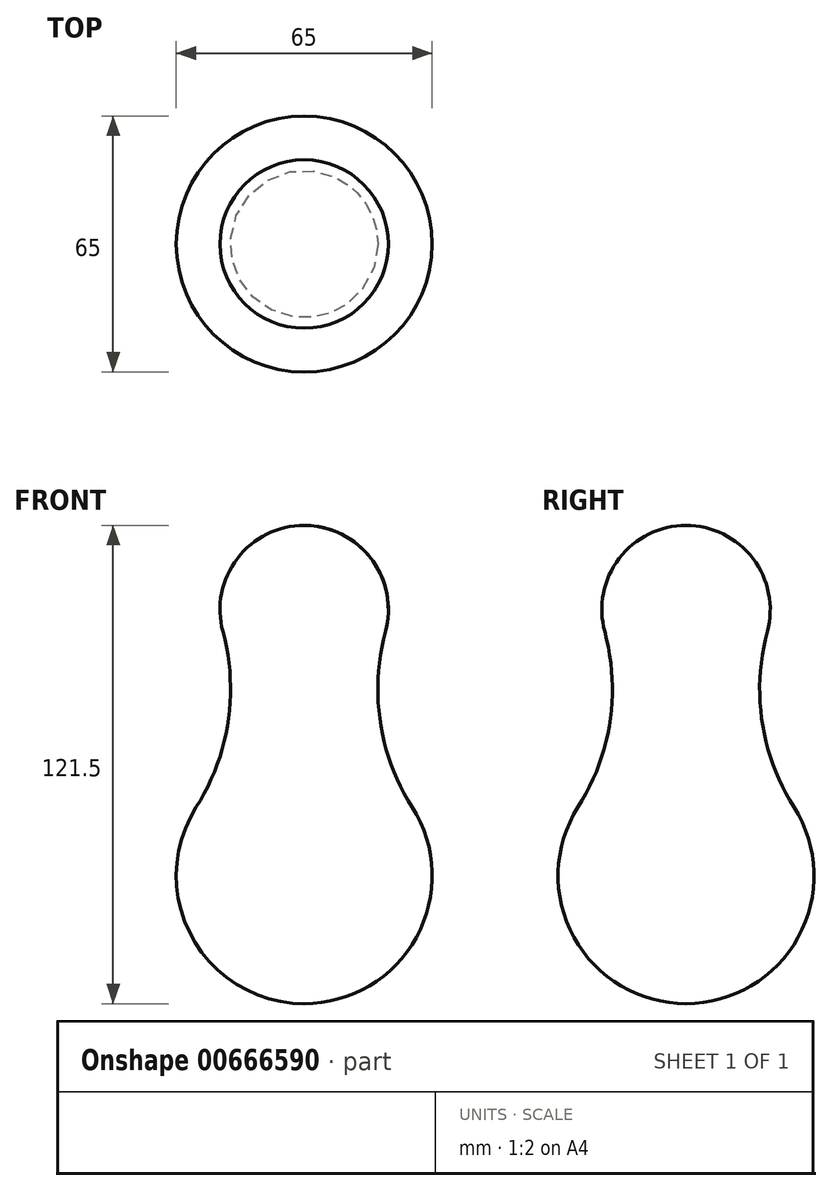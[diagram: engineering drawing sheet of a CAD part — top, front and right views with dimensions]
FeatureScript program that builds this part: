
annotation { "Feature Type Name" : "Feature", "Feature Type Description" : "" }
export const myFeature = defineFeature(function(context is Context, id is Id, definition is map)
    precondition{}
    {
        {
            var Q0;
            Q0=qCreatedBy(makeId("Front.planeOp"),FACE);
            var sketch = newSketch(context, id + "F0", { "sketchPlane" : qUnion([Q0])});
            skArc(sketch, "E0", {"start": v(0, 54.91) * mm, "mid": v(-16.99, 46.52) * mm, "end": v(-20.65, 27.93) * mm});
            skArc(sketch, "E1", {"start": v(-27.43, -16.65) * mm, "mid": v(-28.49, -49.74) * mm, "end": v(0, -66.6) * mm});
            skArc(sketch, "E2", {"start": v(-27.43, -16.65) * mm, "mid": v(-19.34, 4.93) * mm, "end": v(-20.65, 27.93) * mm});
            skLineSegment(sketch, "E3", {"start": v(0, 54.91) * mm, "end": v(0, -66.6) * mm});
            skSolve(sketch);
        }
        {
            var Q0;
            Q0=makeQuery(id+"F0.imprint","IMPRINT",FACE,{"disambiguationData":[TD([[makeQuery(id+"F0.imprint","IMPRINT",EDGE,{"derivedFrom":sQuery(id+"F0.wireOp",EDGE,"E0")}),1.0]])]});
            var Q1;
            Q1=sQuery(id+"F0.wireOp",EDGE,"E3");
            revolve(context, id + "F1", {"entities" : qUnion([Q0]), "axis" : qUnion([Q1]), "revolveType" : RevolveType.FULL});
        }
    });
